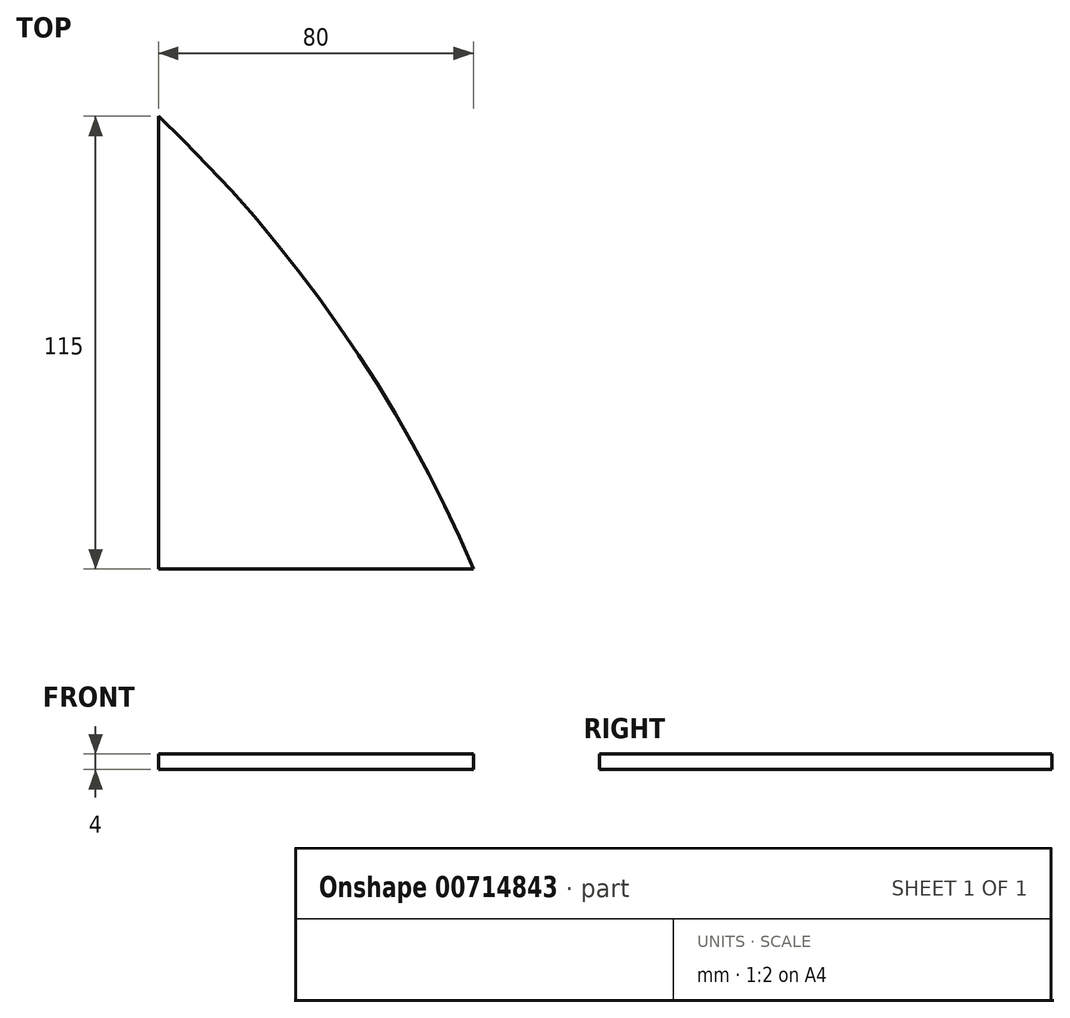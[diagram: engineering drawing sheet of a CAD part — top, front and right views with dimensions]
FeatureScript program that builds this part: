
annotation { "Feature Type Name" : "Feature", "Feature Type Description" : "" }
export const myFeature = defineFeature(function(context is Context, id is Id, definition is map)
    precondition{}
    {
        {
            var Q0;
            Q0=qCreatedBy(makeId("Top.planeOp"),FACE);
            var sketch = newSketch(context, id + "F0", { "sketchPlane" : qUnion([Q0])});
            skLineSegment(sketch, "E0.bottom", {"start": v(-46.91, 41.85) * mm, "end": v(33.09, 41.85) * mm});
            skLineSegment(sketch, "E0.top", {"start": v(-46.91, -73.15) * mm, "end": v(33.09, -73.15) * mm});
            skLineSegment(sketch, "E0.left", {"start": v(-46.91, 41.85) * mm, "end": v(-46.91, -73.15) * mm});
            skLineSegment(sketch, "E0.right", {"start": v(33.09, 41.85) * mm, "end": v(33.09, -73.15) * mm});
            skArc(sketch, "E1", {"start": v(33.09, -73.15) * mm, "mid": v(-0.96, -11.51) * mm, "end": v(-46.91, 41.85) * mm});
            skSolve(sketch);
        }
        {
            var Q0;
            {var subQ1=sQuery(id+"F0.wireOp",EDGE,"E0.left");Q0=makeQuery(id+"F0.imprint","IMPRINT",FACE,{"disambiguationData":[TD([[makeQuery(id+"F0.imprint","IMPRINT",EDGE,{"derivedFrom":subQ1}),1.0]])]});}
            var Q1;
            {var subQ0=sQuery(id+"F0.wireOp",EDGE,"djZaC3i5-zcGr-rptL-fQA0-CZrFzQ3Pm8CA");var subQ1=sQuery(id+"F0.wireOp",EDGE,"O7eMt7TD-QWkj-fa9X-RxE1-PApIbBj8yl93");var subQ3=makeQuery(id+"F0.imprint","INTERSECT",VERTEX,{"derivedFrom":[subQ1,subQ0]});Q1=makeQuery(id+"F0.imprint","IMPRINT",FACE,{"disambiguationData":[TD([[makeQuery(id+"F0.imprint","IMPRINT",EDGE,{"disambiguationData":[TD([[subQ3,-1.0]])],"derivedFrom":subQ1}),1.0]])]});}
            extrude(context, id + "F1", {"entities" : qUnion([Q0, Q1]), "depth" : 4 * mm, "offsetDistance" : 25 * mm});
        }
    });
